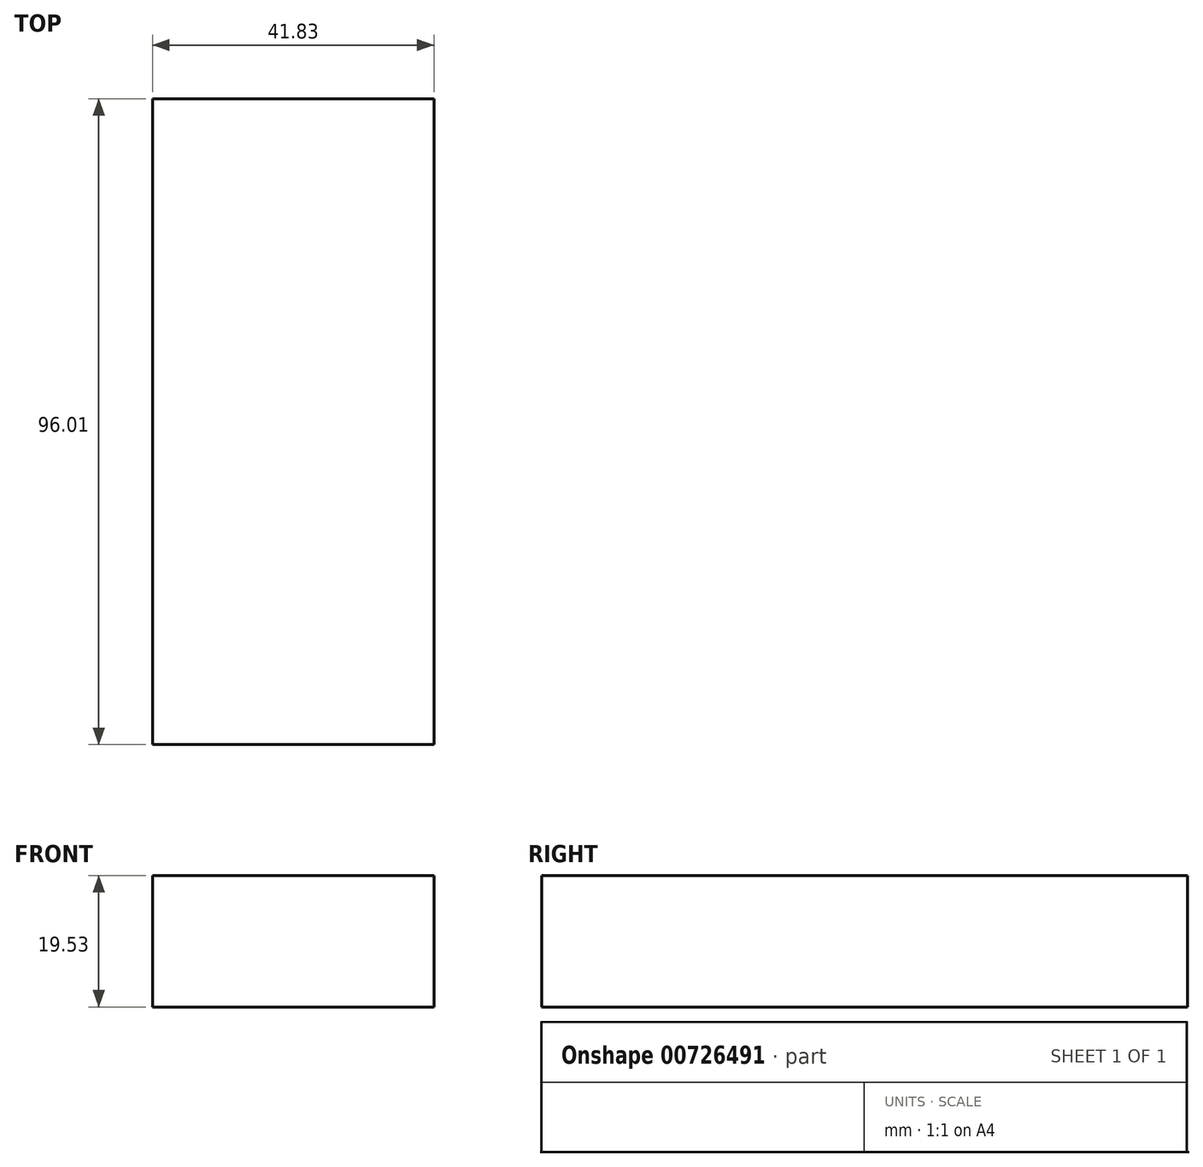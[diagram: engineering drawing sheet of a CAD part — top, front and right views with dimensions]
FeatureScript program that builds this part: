
annotation { "Feature Type Name" : "Feature", "Feature Type Description" : "" }
export const myFeature = defineFeature(function(context is Context, id is Id, definition is map)
    precondition{}
    {
        {
            var Q0;
            Q0=qCreatedBy(makeId("Front.planeOp"),FACE);
            var sketch = newSketch(context, id + "F0", { "sketchPlane" : qUnion([Q0])});
            skLineSegment(sketch, "E0.bottom", {"start": v(-58.1, 44.33) * mm, "end": v(-16.27, 44.33) * mm});
            skLineSegment(sketch, "E0.top", {"start": v(-58.1, 24.8) * mm, "end": v(-16.27, 24.8) * mm});
            skLineSegment(sketch, "E0.left", {"start": v(-58.1, 44.33) * mm, "end": v(-58.1, 24.8) * mm});
            skLineSegment(sketch, "E0.right", {"start": v(-16.27, 44.33) * mm, "end": v(-16.27, 24.8) * mm});
            skSolve(sketch);
        }
        {
            var Q0;
            Q0=makeQuery(id+"F0.imprint","IMPRINT",FACE,{"disambiguationData":[TD([[makeQuery(id+"F0.imprint","IMPRINT",EDGE,{"derivedFrom":sQuery(id+"F0.wireOp",EDGE,"E0.bottom")}),-1.0]])]});
            extrude(context, id + "F1", {"entities" : qUnion([Q0]), "depth" : 96.01 * mm, "offsetDistance" : 25.4 * mm});
        }
    });
